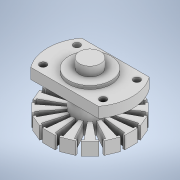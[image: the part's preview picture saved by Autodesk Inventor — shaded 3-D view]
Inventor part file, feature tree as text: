
AUTODESK INVENTOR PART (.ipt)
format: ipt  version: 2020 (Build 240168000, 168)  size: 257,024 bytes
history: native  units: mm
features: sketch x8, extrude x7, hole x1, pattern_circular x1, projected_geometry x1
ambient origin geometry x8: Origin, YZ Plane, XZ Plane, XY Plane, X Axis, Y Axis, Z Axis, Center Point
bodies: Solid1 (feature_tree)
feature tree (18):
  extrude  "Extrusion1"  Depth=12.0mm
  extrude  "Extrusion2"  Depth=2.5mm TaperAngle=0.0deg
  extrude  "Extrusion3"  Depth=0.8mm TaperAngle=0.0deg
  extrude  "Extrusion4"  Depth=3.0mm TaperAngle=0.0deg
  hole  "Hole1"  [1 undecoded]
  extrude  "Extrusion5"  Depth=14.2mm
  extrude  "Extrusion6"  Depth=2.0mm
  pattern_circular  "Circular Pattern1"  [2 undecoded]
  extrude  "Extrusion7"  Depth=0.5mm
  sketch  "Sketch1"  dims[d0=20.0mm d1=12.0mm]
  sketch  "Sketch2"  dims[d2=22.0mm d3=2.5mm d4=0.0mm]
  sketch  "Sketch3"  dims[d5=10.0mm d6=0.8mm d7=0.0mm]
  sketch  "Sketch4"  dims[d8=5.0mm d9=3.0mm d10=0.0mm]
  sketch  "Sketch5"  dims[d11=7.7mm d12=4.8mm d13=0.0mm]
  sketch  "Sketch6"  dims[d14=8.0mm d15=14.2mm]
  sketch  "Sketch7"  dims[d16=1.6mm d17=6.0mm d18=4.0mm d19=2.0mm d20=90.0deg d21=17.0mm d22=0.0mm d23=9.5mm]
  projected_geometry  "Projected Loop1"
  sketch  "Sketch8"  dims[d24=0.5mm d25=3.0mm d26=0.5mm d27=0.5mm d28=3.0mm d29=0.0mm d30=3.0mm d31=0.0mm d32=160.0mm d33=360.0deg d35=3.5mm d36=5.0mm d37=0.0mm]
note: 3 required parameter values undecoded (feature->parameter linkage not recoverable at this tier; creation-order binding heuristic only, values carry confidence <= 0.55)
